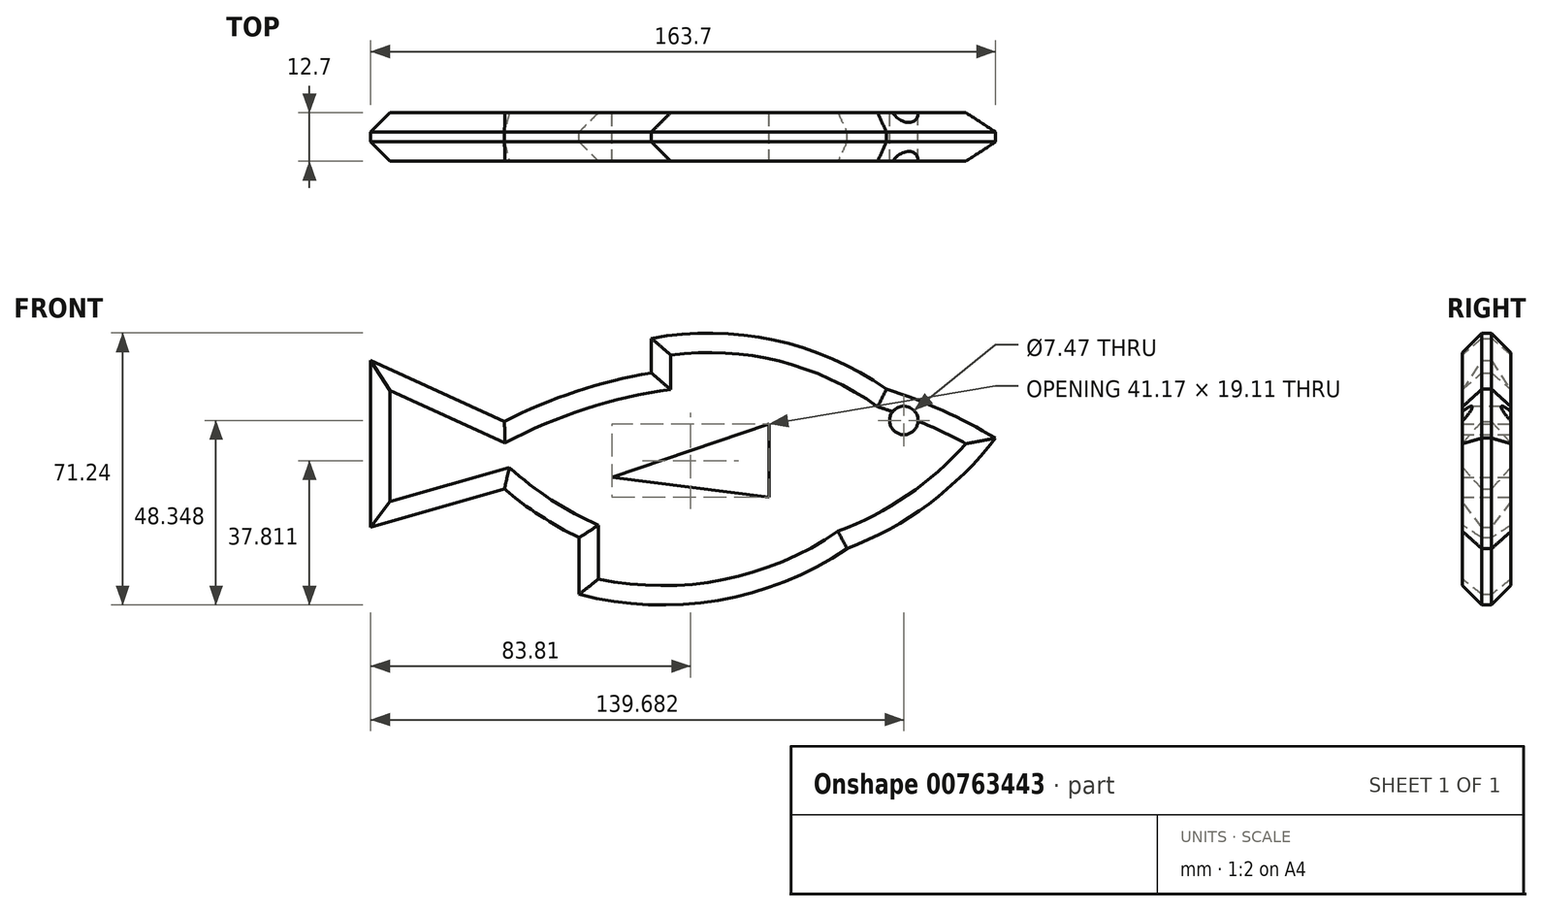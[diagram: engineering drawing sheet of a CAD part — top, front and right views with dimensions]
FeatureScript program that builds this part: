
annotation { "Feature Type Name" : "Feature", "Feature Type Description" : "" }
export const myFeature = defineFeature(function(context is Context, id is Id, definition is map)
    precondition{}
    {
        {
            var Q0;
            Q0=qCreatedBy(makeId("Front.planeOp"),FACE);
            var sketch = newSketch(context, id + "F0", { "sketchPlane" : qUnion([Q0])});
            skArc(sketch, "E0", {"start": v(68.74, 10.3) * mm, "mid": v(54.82, 17.57) * mm, "end": v(40.15, 23.15) * mm});
            skArc(sketch, "E1", {"start": v(-59.9, -3) * mm, "mid": v(-50.55, -10) * mm, "end": v(-40.35, -15.74) * mm});
            skCircle(sketch, "E2", {"center": v(44.72, 14.95) * mm, "radius": 3.73 * mm});
            skLineSegment(sketch, "E3", {"start": v(9.43, 13.97) * mm, "end": v(9.43, -5.15) * mm});
            skLineSegment(sketch, "E4", {"start": v(9.43, 13.97) * mm, "end": v(-31.73, 0) * mm});
            skLineSegment(sketch, "E5", {"start": v(-31.73, 0) * mm, "end": v(9.43, -5.15) * mm});
            skLineSegment(sketch, "E6", {"start": v(-59.9, 14.67) * mm, "end": v(-94.96, 30.63) * mm});
            skLineSegment(sketch, "E7", {"start": v(-59.9, -3) * mm, "end": v(-94.96, -12.99) * mm});
            skLineSegment(sketch, "E8", {"start": v(-94.96, -12.99) * mm, "end": v(-94.96, 30.63) * mm});
            skLineSegment(sketch, "E9", {"start": v(-21.44, 27.4) * mm, "end": v(-21.44, 36.44) * mm});
            skArc(sketch, "E10", {"start": v(40.15, 23.15) * mm, "mid": v(10.7, 36.01) * mm, "end": v(-21.44, 36.44) * mm});
            skArc(sketch, "E11.trimOffspring", {"start": v(-21.44, 27.4) * mm, "mid": v(-41.16, 22.51) * mm, "end": v(-59.9, 14.67) * mm});
            skLineSegment(sketch, "E12", {"start": v(-40.35, -15.74) * mm, "end": v(-40.35, -30.58) * mm});
            skArc(sketch, "E13", {"start": v(-40.35, -30.58) * mm, "mid": v(-3.97, -32.18) * mm, "end": v(29.83, -18.64) * mm});
            skArc(sketch, "E14.trimOffspring", {"start": v(29.83, -18.64) * mm, "mid": v(51.29, -6.87) * mm, "end": v(68.74, 10.3) * mm});
            skSolve(sketch);
        }
        {
            var Q0;
            Q0=makeQuery(id+"F0.imprint","IMPRINT",FACE,{"disambiguationData":[TD([[makeQuery(id+"F0.imprint","IMPRINT",EDGE,{"derivedFrom":sQuery(id+"F0.wireOp",EDGE,"E0")}),1.0]])]});
            extrude(context, id + "F1", {"entities" : qUnion([Q0]), "depth" : 12.7 * mm, "offsetDistance" : 25.4 * mm});
        }
        {
            var Q0;
            Q0=makeQuery(id+"F1.opExtrude","CAP_EDGE",EDGE,{"disambiguationData":[OSD([sQuery(id+"F0.wireOp",EDGE,"E11.trimOffspring")])],"isStart":false});
            var Q1;
            Q1=makeQuery(id+"F1.opExtrude","CAP_EDGE",EDGE,{"disambiguationData":[OSD([sQuery(id+"F0.wireOp",EDGE,"E6")])],"isStart":false});
            var Q2;
            Q2=makeQuery(id+"F1.opExtrude","CAP_EDGE",EDGE,{"disambiguationData":[OSD([sQuery(id+"F0.wireOp",EDGE,"E8")])],"isStart":false});
            var Q3;
            Q3=makeQuery(id+"F1.opExtrude","CAP_EDGE",EDGE,{"disambiguationData":[OSD([sQuery(id+"F0.wireOp",EDGE,"E7")])],"isStart":false});
            var Q4;
            Q4=makeQuery(id+"F1.opExtrude","CAP_EDGE",EDGE,{"disambiguationData":[OSD([sQuery(id+"F0.wireOp",EDGE,"E1")])],"isStart":false});
            var Q5;
            Q5=makeQuery(id+"F1.opExtrude","CAP_EDGE",EDGE,{"disambiguationData":[OSD([sQuery(id+"F0.wireOp",EDGE,"E12")])],"isStart":false});
            var Q6;
            Q6=makeQuery(id+"F1.opExtrude","CAP_EDGE",EDGE,{"disambiguationData":[OSD([sQuery(id+"F0.wireOp",EDGE,"E13")])],"isStart":false});
            var Q7;
            Q7=makeQuery(id+"F1.opExtrude","CAP_EDGE",EDGE,{"disambiguationData":[OSD([sQuery(id+"F0.wireOp",EDGE,"E14.trimOffspring")])],"isStart":false});
            var Q8;
            Q8=makeQuery(id+"F1.opExtrude","CAP_EDGE",EDGE,{"disambiguationData":[OSD([sQuery(id+"F0.wireOp",EDGE,"E0")])],"isStart":false});
            var Q9;
            Q9=makeQuery(id+"F1.opExtrude","CAP_EDGE",EDGE,{"disambiguationData":[OSD([sQuery(id+"F0.wireOp",EDGE,"E10")])],"isStart":false});
            var Q10;
            Q10=makeQuery(id+"F1.opExtrude","CAP_EDGE",EDGE,{"disambiguationData":[OSD([sQuery(id+"F0.wireOp",EDGE,"E9")])],"isStart":false});
            chamfer(context, id + "F2", {"entities" : qUnion([Q0, Q1, Q2, Q3, Q4, Q5, Q6, Q7, Q8, Q9, Q10]), "width" : 5.08 * mm, "tangentPropagation" : true});
        }
        {
            var Q0;
            Q0=makeQuery(id+"F1.opExtrude","CAP_EDGE",EDGE,{"disambiguationData":[OSD([sQuery(id+"F0.wireOp",EDGE,"E13")])],"isStart":true});
            var Q1;
            Q1=makeQuery(id+"F1.opExtrude","CAP_EDGE",EDGE,{"disambiguationData":[OSD([sQuery(id+"F0.wireOp",EDGE,"E14.trimOffspring")])],"isStart":true});
            var Q2;
            Q2=makeQuery(id+"F1.opExtrude","CAP_EDGE",EDGE,{"disambiguationData":[OSD([sQuery(id+"F0.wireOp",EDGE,"E0")])],"isStart":true});
            var Q3;
            Q3=makeQuery(id+"F1.opExtrude","CAP_EDGE",EDGE,{"disambiguationData":[OSD([sQuery(id+"F0.wireOp",EDGE,"E10")])],"isStart":true});
            var Q4;
            Q4=makeQuery(id+"F1.opExtrude","CAP_EDGE",EDGE,{"disambiguationData":[OSD([sQuery(id+"F0.wireOp",EDGE,"E9")])],"isStart":true});
            var Q5;
            Q5=makeQuery(id+"F1.opExtrude","CAP_EDGE",EDGE,{"disambiguationData":[OSD([sQuery(id+"F0.wireOp",EDGE,"E11.trimOffspring")])],"isStart":true});
            var Q6;
            Q6=makeQuery(id+"F1.opExtrude","CAP_EDGE",EDGE,{"disambiguationData":[OSD([sQuery(id+"F0.wireOp",EDGE,"E6")])],"isStart":true});
            var Q7;
            Q7=makeQuery(id+"F1.opExtrude","CAP_EDGE",EDGE,{"disambiguationData":[OSD([sQuery(id+"F0.wireOp",EDGE,"E1")])],"isStart":true});
            var Q8;
            Q8=makeQuery(id+"F1.opExtrude","CAP_EDGE",EDGE,{"disambiguationData":[OSD([sQuery(id+"F0.wireOp",EDGE,"E7")])],"isStart":true});
            var Q9;
            Q9=makeQuery(id+"F1.opExtrude","CAP_EDGE",EDGE,{"disambiguationData":[OSD([sQuery(id+"F0.wireOp",EDGE,"E12")])],"isStart":true});
            var Q10;
            Q10=makeQuery(id+"F1.opExtrude","CAP_EDGE",EDGE,{"disambiguationData":[OSD([sQuery(id+"F0.wireOp",EDGE,"E8")])],"isStart":true});
            chamfer(context, id + "F3", {"entities" : qUnion([Q0, Q1, Q2, Q3, Q4, Q5, Q6, Q7, Q8, Q9, Q10]), "width" : 5.08 * mm, "tangentPropagation" : true});
        }
    });
